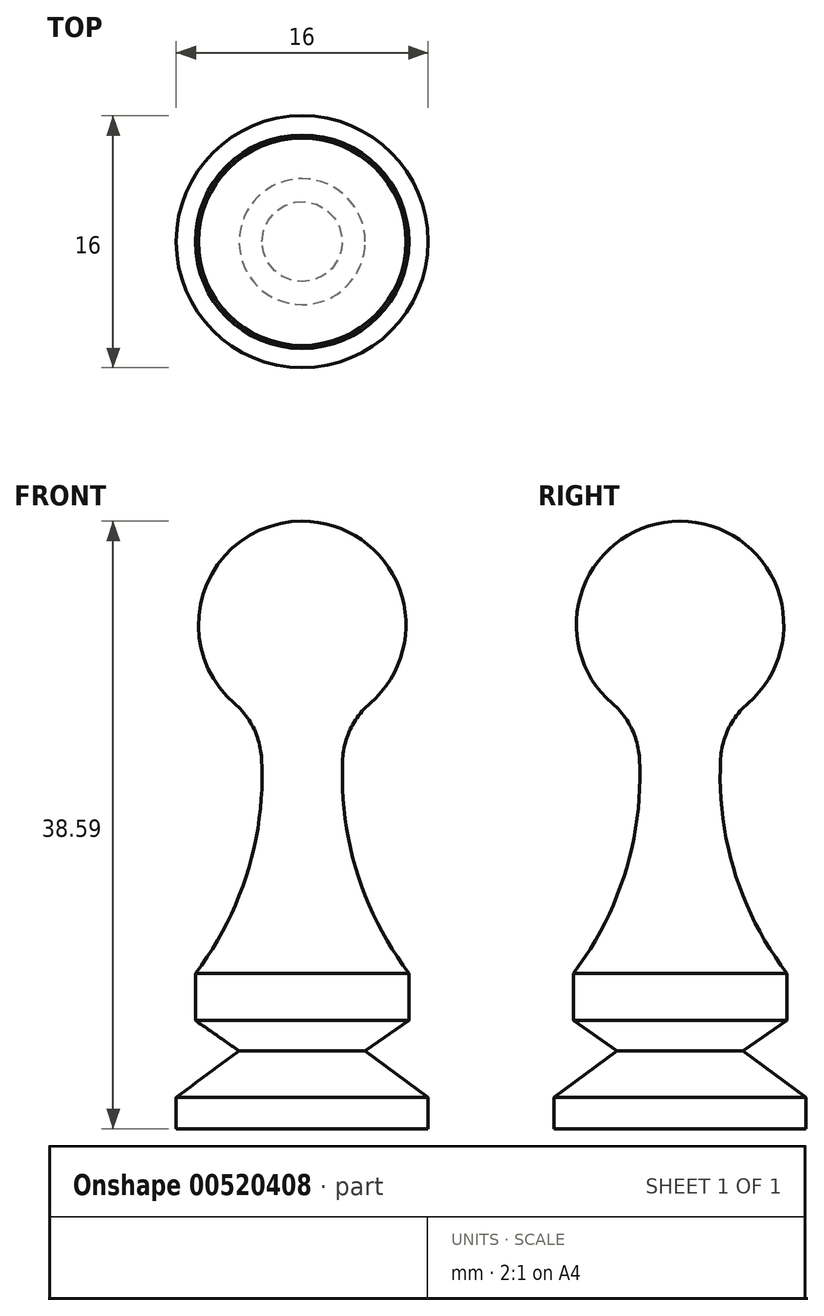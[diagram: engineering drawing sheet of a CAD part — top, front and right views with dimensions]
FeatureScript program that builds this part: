
annotation { "Feature Type Name" : "Feature", "Feature Type Description" : "" }
export const myFeature = defineFeature(function(context is Context, id is Id, definition is map)
    precondition{}
    {
        {
            var Q0;
            Q0=qCreatedBy(makeId("Front.planeOp"),FACE);
            var sketch = newSketch(context, id + "F0", { "sketchPlane" : qUnion([Q0])});
            skLineSegment(sketch, "E0", {"start": v(0, 0) * mm, "end": v(0, 32) * mm});
            skLineSegment(sketch, "E1", {"start": v(0, 0) * mm, "end": v(-8, 0) * mm});
            skLineSegment(sketch, "E2", {"start": v(-8, 0) * mm, "end": v(-8, 2) * mm});
            skLineSegment(sketch, "E3", {"start": v(-6.78, 9.87) * mm, "end": v(-6.78, 6.87) * mm});
            skLineSegment(sketch, "E4", {"start": v(0, 9.87) * mm, "end": v(0, 0) * mm});
            skLineSegment(sketch, "E5", {"start": v(0, 0) * mm, "end": v(0, 26.07) * mm});
            skArc(sketch, "E6", {"start": v(0, 38.59) * mm, "mid": v(-6.42, 33.47) * mm, "end": v(-2.87, 26.07) * mm});
            skLineSegment(sketch, "E7", {"start": v(0, 32) * mm, "end": v(0, 38.59) * mm});
            skArc(sketch, "E8", {"start": v(-6.78, 9.87) * mm, "mid": v(-3.12, 17.56) * mm, "end": v(-2.87, 26.07) * mm});
            skPoint(sketch, "E9.endSnap0", {"position": v(0, 4.93) * mm});
            skLineSegment(sketch, "E10", {"start": v(-4, 4.93) * mm, "end": v(-6.78, 6.87) * mm});
            skLineSegment(sketch, "E11", {"start": v(-8, 2) * mm, "end": v(-4, 4.93) * mm});
            skSolve(sketch);
        }
        {
            var Q0;
            {var subQ1=sQuery(id+"F0.wireOp",EDGE,"E0");Q0=makeQuery(id+"F0.imprint","IMPRINT",FACE,{"disambiguationData":[TD([[makeQuery(id+"F0.imprint","IMPRINT",EDGE,{"derivedFrom":subQ1}),1.0]])]});}
            var Q1;
            Q1=sQuery(id+"F0.wireOp",EDGE,"E7");
            revolve(context, id + "F1", {"entities" : qUnion([Q0]), "axis" : qUnion([Q1]), "revolveType" : RevolveType.FULL});
        }
        {
            var Q0;
            Q0=makeQuery(id+"F1.opRevolve","SWEPT_EDGE",EDGE,{"disambiguationData":[OSD([sQuery(id+"F0.wireOp",EDGE,"E6"),sQuery(id+"F0.wireOp",EDGE,"E8")])]});
            var Q1;
            Q1=makeQuery(id+"F1.opRevolve","SWEPT_FACE",FACE,{"disambiguationData":[OSD([sQuery(id+"F0.wireOp",EDGE,"E6")])]});
            fillet(context, id + "F2", {"entities" : qUnion([Q0, Q1]), "radius" : 5 * mm, "tangentPropagation" : true, "allowEdgeOverflow" : false});
        }
    });
